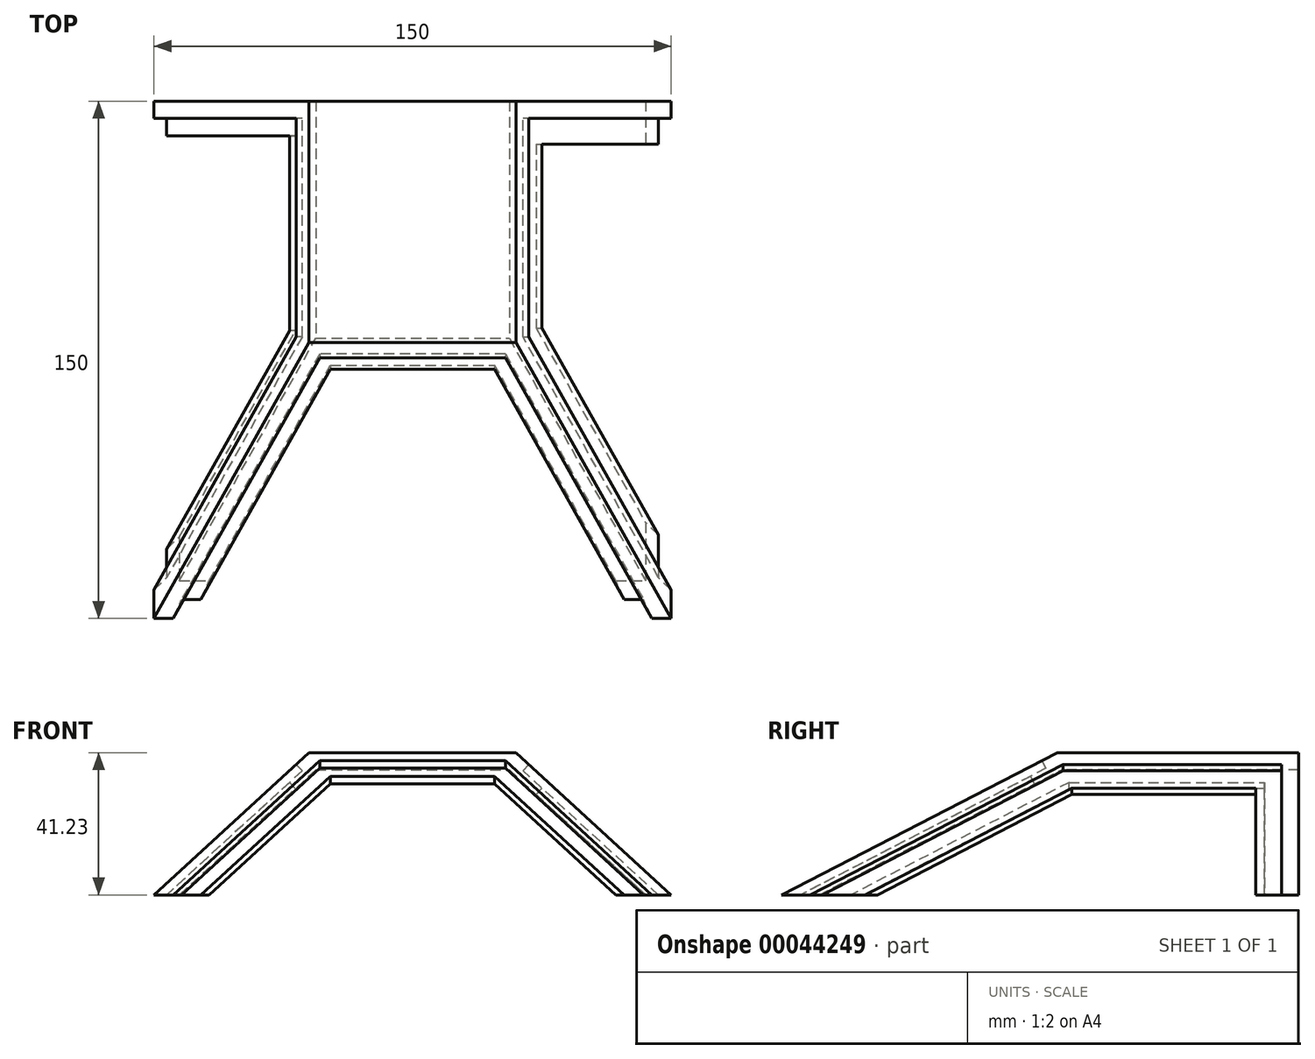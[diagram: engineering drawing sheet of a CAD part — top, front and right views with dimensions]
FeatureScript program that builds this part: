
annotation { "Feature Type Name" : "Feature", "Feature Type Description" : "" }
export const myFeature = defineFeature(function(context is Context, id is Id, definition is map)
    precondition{}
    {
        {
            var Q0;
            Q0=qCreatedBy(makeId("Top.planeOp"),FACE);
            var sketch = newSketch(context, id + "F0", { "sketchPlane" : qUnion([Q0])});
            skLineSegment(sketch, "E0.bottom", {"start": v(-75, 75) * mm, "end": v(75, 75) * mm});
            skLineSegment(sketch, "E0.top", {"start": v(-75, -75) * mm, "end": v(75, -75) * mm});
            skLineSegment(sketch, "E0.left", {"start": v(-75, 75) * mm, "end": v(-75, -75) * mm});
            skLineSegment(sketch, "E0.right", {"start": v(75, 75) * mm, "end": v(75, -75) * mm});
            skPoint(sketch, "E0.middle", {"position": v(0, 0) * mm});
            skLineSegment(sketch, "E1.bottom", {"start": v(30, 75) * mm, "end": v(-30, 75) * mm, "construction": true});
            skLineSegment(sketch, "E1.top", {"start": v(30, 5) * mm, "end": v(-30, 5) * mm, "construction": true});
            skLineSegment(sketch, "E1.left", {"start": v(30, 75) * mm, "end": v(30, 5) * mm, "construction": true});
            skLineSegment(sketch, "E1.right", {"start": v(-30, 75) * mm, "end": v(-30, 5) * mm, "construction": true});
            skPoint(sketch, "E1.middle", {"position": v(0, 40) * mm});
            skPoint(sketch, "E1.middle.positionSnap0", {"position": v(0, 75) * mm});
            skPoint(sketch, "E1.centerSnap0", {"position": v(0, 75) * mm});
            skLineSegment(sketch, "E2", {"start": v(-30, 40) * mm, "end": v(-75, 40) * mm, "construction": true});
            skLineSegment(sketch, "E3", {"start": v(30, 40) * mm, "end": v(75, 40) * mm, "construction": true});
            skLineSegment(sketch, "E4", {"start": v(30, 5) * mm, "end": v(75, -75) * mm, "construction": true});
            skSolve(sketch);
        }
        {
            var Q0;
            Q0=qCreatedBy(makeId("Right.planeOp"),FACE);
            var sketch = newSketch(context, id + "F1", { "sketchPlane" : qUnion([Q0])});
            skLineSegment(sketch, "E5.0", {"start": v(5, 0) * mm, "end": v(-75, 0) * mm, "construction": true});
            skLineSegment(sketch, "E6", {"start": v(-75, 0) * mm, "end": v(5, 41.23) * mm, "construction": true});
            skLineSegment(sketch, "E7", {"start": v(5, 41.23) * mm, "end": v(5, 0) * mm, "construction": true});
            skSolve(sketch);
        }
        {
            var Q0;
            Q0=sQuery(id+"F1.wireOp",EDGE,"E7");
            var Q1;
            Q1=sQuery(id+"F1.wireOp",VERTEX,"E6.end");
            cPlane(context, id + "F2", {"entities" : qUnion([Q0, Q1]), "cplaneType" : CPlaneType.CURVE_POINT, "offset" : 25 * mm, "width" : 150 * mm, "height" : 150 * mm});
        }
        {
            var Q0;
            Q0=qCreatedBy(id+"F2.planeOp",FACE);
            var sketch = newSketch(context, id + "F3", { "sketchPlane" : qUnion([Q0])});
            skLineSegment(sketch, "E8.0", {"start": v(-30, -75) * mm, "end": v(-30, -5) * mm});
            skLineSegment(sketch, "E9.0", {"start": v(30, -5) * mm, "end": v(-30, -5) * mm});
            skLineSegment(sketch, "E10.0", {"start": v(30, -75) * mm, "end": v(30, -5) * mm});
            skLineSegment(sketch, "E11.0", {"start": v(-75, -75) * mm, "end": v(75, -75) * mm});
            skSolve(sketch);
        }
        {
            var Q0;
            Q0=makeQuery(id+"F0.imprint","IMPRINT",FACE,{"disambiguationData":[TD([[makeQuery(id+"F0.imprint","IMPRINT",EDGE,{"derivedFrom":sQuery(id+"F0.wireOp",EDGE,"E0.bottom")}),-1.0]])]});
            var Q1;
            {var subQ0=sQuery(id+"F3.wireOp",EDGE,"E8.0");Q1=makeQuery(id+"F3.imprint","IMPRINT",FACE,{"disambiguationData":[TD([[makeQuery(id+"F3.imprint","IMPRINT",EDGE,{"derivedFrom":subQ0}),-1.0]])]});}
            var Q2;
            Q2=sQuery(id+"F0.wireOp",VERTEX,"E0.left.end");
            var Q3;
            Q3=sQuery(id+"F3.wireOp",VERTEX,"E8.0.start");
            loft(context, id + "F4", {"sheetProfilesArray" : [{ "sheetProfileEntities" : qUnion([Q0]) }, { "sheetProfileEntities" : qUnion([Q1]) }], "connections" : [{ "connectionEntities" : qUnion([Q2, Q3]), "connectionEdgeQueries" : qUnion([]), "connectionEdgeParameters" : [] }]});
        }
        {
            var Q0;
            Q0=makeQuery(id+"F4.opLoft","SWEPT_FACE",FACE,{"disambiguationData":[OSD([sQuery(id+"F0.wireOp",EDGE,"E0.bottom"),sQuery(id+"F0.wireOp",EDGE,"E0.left"),sQuery(id+"F0.wireOp",EDGE,"E0.right"),sQuery(id+"F3.wireOp",EDGE,"E8.0"),sQuery(id+"F3.wireOp",EDGE,"E10.0"),sQuery(id+"F3.wireOp",EDGE,"E11.0")])]});
            var Q1;
            Q1=makeQuery(id+"F4.opLoft","CAP_FACE",FACE,{"disambiguationData":[OSD([makeQuery(id+"F0.imprint","IMPRINT",FACE,{"disambiguationData":[TD([[makeQuery(id+"F0.imprint","IMPRINT",EDGE,{"derivedFrom":sQuery(id+"F0.wireOp",EDGE,"E0.bottom")}),-1.0]])]})])],"isStart":true});
            shell(context, id + "F5", {"entities" : qUnion([Q0, Q1]), "thickness" : 5 * mm});
        }
        {
            var Q0;
            Q0=makeQuery(id+"F4.opLoft","SWEPT_FACE",FACE,{"disambiguationData":[OSD([sQuery(id+"F0.wireOp",EDGE,"E0.bottom"),sQuery(id+"F0.wireOp",EDGE,"E0.top"),sQuery(id+"F0.wireOp",EDGE,"E0.right"),sQuery(id+"F3.wireOp",EDGE,"E9.0"),sQuery(id+"F3.wireOp",EDGE,"E10.0"),sQuery(id+"F3.wireOp",EDGE,"E11.0")])]});
            var sketch = newSketch(context, id + "F6", { "sketchPlane" : qUnion([Q0])});
            skLineSegment(sketch, "E12.0", {"start": v(55.3, 70) * mm, "end": v(-0.73, 70) * mm});
            skLineSegment(sketch, "E12.1", {"start": v(-0.73, 6.69) * mm, "end": v(-0.73, 70) * mm});
            skLineSegment(sketch, "E12.2", {"start": v(59.27, -71.97) * mm, "end": v(-0.73, 6.69) * mm});
            skLineSegment(sketch, "E13.0", {"start": v(55.3, 62.5) * mm, "end": v(6.77, 62.5) * mm});
            skLineSegment(sketch, "E13.1", {"start": v(6.77, 9.22) * mm, "end": v(6.77, 62.5) * mm});
            skLineSegment(sketch, "E13.2", {"start": v(65.24, -67.42) * mm, "end": v(6.77, 9.22) * mm});
            skSolve(sketch);
        }
        {
            var Q0;
            {var subQ7=sQuery(id+"F6.wireOp",EDGE,"E12.0");Q0=makeQuery(id+"F6.imprint","IMPRINT",FACE,{"disambiguationData":[TD([[makeQuery(id+"F6.imprint","IMPRINT",EDGE,{"derivedFrom":subQ7}),1.0]])]});}
            var Q1;
            Q1=makeQuery(id+"F5.opShell","OFFSET_FACE",FACE,{"disambiguationData":[OSD([sQuery(id+"F0.wireOp",EDGE,"E0.bottom"),sQuery(id+"F0.wireOp",EDGE,"E0.top"),sQuery(id+"F0.wireOp",EDGE,"E0.right"),sQuery(id+"F3.wireOp",EDGE,"E9.0"),sQuery(id+"F3.wireOp",EDGE,"E10.0"),sQuery(id+"F3.wireOp",EDGE,"E11.0")])]});
            extrude(context, id + "F7", {"entities" : qUnion([Q0]), "operationType" : NewBodyOperationType.REMOVE, "endBound" : BoundingType.UP_TO_SURFACE, "oppositeDirection" : true, "depth" : 25 * mm, "endBoundEntityFace" : qUnion([Q1]), "hasOffset" : true, "offsetDistance" : 2.5 * mm});
        }
        {
            var Q0;
            {var subQ0=sQuery(id+"F0.wireOp",EDGE,"E0.bottom");var subQ1=sQuery(id+"F0.wireOp",EDGE,"E0.top");var subQ2=sQuery(id+"F0.wireOp",EDGE,"E0.right");Q0=makeQuery(id+"F7.boolean.opBoolean","SPLIT",FACE,{"disambiguationData":[TD([makeQuery(id+"F7.opExtrude","SWEPT_FACE",FACE,{"disambiguationData":[OSD([sQuery(id+"F6.wireOp",EDGE,"E13.0")])]})])],"derivedFrom":makeQuery(id+"F4.opLoft","SWEPT_FACE",FACE,{"disambiguationData":[OSD([subQ0,subQ1,subQ2,sQuery(id+"F3.wireOp",EDGE,"E9.0"),sQuery(id+"F3.wireOp",EDGE,"E10.0"),sQuery(id+"F3.wireOp",EDGE,"E11.0")])]})});}
            extrude(context, id + "F8", {"entities" : qUnion([Q0]), "operationType" : NewBodyOperationType.REMOVE, "endBound" : BoundingType.THROUGH_ALL, "oppositeDirection" : true, "depth" : 25 * mm, "offsetDistance" : 25 * mm});
        }
        {
            var Q0;
            Q0=makeQuery(id+"F4.opLoft","SWEPT_FACE",FACE,{"disambiguationData":[OSD([sQuery(id+"F0.wireOp",EDGE,"E0.top"),sQuery(id+"F0.wireOp",EDGE,"E0.left"),sQuery(id+"F0.wireOp",EDGE,"E0.right"),sQuery(id+"F3.wireOp",EDGE,"E8.0"),sQuery(id+"F3.wireOp",EDGE,"E9.0"),sQuery(id+"F3.wireOp",EDGE,"E10.0")])]});
            var sketch = newSketch(context, id + "F9", { "sketchPlane" : qUnion([Q0])});
            skLineSegment(sketch, "E14.0", {"start": v(70.53, -68.9) * mm, "end": v(26.9, 18.33) * mm});
            skLineSegment(sketch, "E14.1", {"start": v(-26.9, 18.33) * mm, "end": v(26.9, 18.33) * mm});
            skLineSegment(sketch, "E14.2", {"start": v(-70.53, -68.9) * mm, "end": v(-26.9, 18.33) * mm});
            skLineSegment(sketch, "E15.0", {"start": v(66.06, -71.14) * mm, "end": v(23.82, 13.33) * mm});
            skLineSegment(sketch, "E15.1", {"start": v(-23.82, 13.33) * mm, "end": v(23.82, 13.33) * mm});
            skLineSegment(sketch, "E15.2", {"start": v(-66.06, -71.14) * mm, "end": v(-23.82, 13.33) * mm});
            skSolve(sketch);
        }
        {
            var Q0;
            {var subQ0=sQuery(id+"F9.wireOp",EDGE,"E15.1");Q0=makeQuery(id+"F9.imprint","IMPRINT",FACE,{"disambiguationData":[TD([[makeQuery(id+"F9.imprint","IMPRINT",EDGE,{"derivedFrom":subQ0}),-1.0]])]});}
            extrude(context, id + "F10", {"entities" : qUnion([Q0]), "operationType" : NewBodyOperationType.REMOVE, "endBound" : BoundingType.THROUGH_ALL, "oppositeDirection" : true, "depth" : 25 * mm, "offsetDistance" : 25 * mm});
        }
        {
            var Q0;
            {var subQ5=sQuery(id+"F9.wireOp",EDGE,"E14.1");Q0=makeQuery(id+"F9.imprint","IMPRINT",FACE,{"disambiguationData":[TD([[makeQuery(id+"F9.imprint","IMPRINT",EDGE,{"derivedFrom":subQ5}),-1.0]])]});}
            var Q1;
            Q1=makeQuery(id+"F5.opShell","OFFSET_FACE",FACE,{"disambiguationData":[OSD([sQuery(id+"F0.wireOp",EDGE,"E0.top"),sQuery(id+"F0.wireOp",EDGE,"E0.left"),sQuery(id+"F0.wireOp",EDGE,"E0.right"),sQuery(id+"F3.wireOp",EDGE,"E8.0"),sQuery(id+"F3.wireOp",EDGE,"E9.0"),sQuery(id+"F3.wireOp",EDGE,"E10.0")])]});
            extrude(context, id + "F11", {"entities" : qUnion([Q0]), "operationType" : NewBodyOperationType.REMOVE, "endBound" : BoundingType.UP_TO_SURFACE, "oppositeDirection" : true, "depth" : 25 * mm, "endBoundEntityFace" : qUnion([Q1]), "hasOffset" : true, "offsetDistance" : 2.5 * mm});
        }
        {
            var Q0;
            Q0=makeQuery(id+"F4.opLoft","SWEPT_FACE",FACE,{"disambiguationData":[OSD([sQuery(id+"F0.wireOp",EDGE,"E0.bottom"),sQuery(id+"F0.wireOp",EDGE,"E0.top"),sQuery(id+"F0.wireOp",EDGE,"E0.left"),sQuery(id+"F3.wireOp",EDGE,"E8.0"),sQuery(id+"F3.wireOp",EDGE,"E9.0"),sQuery(id+"F3.wireOp",EDGE,"E11.0")])]});
            var sketch = newSketch(context, id + "F12", { "sketchPlane" : qUnion([Q0])});
            skLineSegment(sketch, "E16.0", {"start": v(-59.27, -71.97) * mm, "end": v(0.73, 6.69) * mm});
            skLineSegment(sketch, "E16.1", {"start": v(0.73, 70) * mm, "end": v(0.73, 6.69) * mm});
            skLineSegment(sketch, "E16.2", {"start": v(-55.3, 70) * mm, "end": v(0.73, 70) * mm});
            skLineSegment(sketch, "E17.0", {"start": v(-63.25, -68.93) * mm, "end": v(-4.27, 8.38) * mm});
            skLineSegment(sketch, "E17.1", {"start": v(-4.27, 65) * mm, "end": v(-4.27, 8.38) * mm});
            skLineSegment(sketch, "E17.2", {"start": v(-55.3, 65) * mm, "end": v(-4.27, 65) * mm});
            skSolve(sketch);
        }
        {
            var Q0;
            {var subQ7=sQuery(id+"F12.wireOp",EDGE,"E16.1");Q0=makeQuery(id+"F12.imprint","IMPRINT",FACE,{"disambiguationData":[TD([[makeQuery(id+"F12.imprint","IMPRINT",EDGE,{"derivedFrom":subQ7}),-1.0]])]});}
            var Q1;
            Q1=makeQuery(id+"F5.opShell","OFFSET_FACE",FACE,{"disambiguationData":[OSD([sQuery(id+"F0.wireOp",EDGE,"E0.bottom"),sQuery(id+"F0.wireOp",EDGE,"E0.top"),sQuery(id+"F0.wireOp",EDGE,"E0.left"),sQuery(id+"F3.wireOp",EDGE,"E8.0"),sQuery(id+"F3.wireOp",EDGE,"E9.0"),sQuery(id+"F3.wireOp",EDGE,"E11.0")])]});
            extrude(context, id + "F13", {"entities" : qUnion([Q0]), "operationType" : NewBodyOperationType.REMOVE, "endBound" : BoundingType.UP_TO_SURFACE, "oppositeDirection" : true, "depth" : 25 * mm, "endBoundEntityFace" : qUnion([Q1]), "hasOffset" : true, "offsetDistance" : 2.5 * mm});
        }
        {
            var Q0;
            {var subQ0=sQuery(id+"F0.wireOp",EDGE,"E0.bottom");var subQ1=sQuery(id+"F0.wireOp",EDGE,"E0.top");var subQ2=sQuery(id+"F0.wireOp",EDGE,"E0.left");Q0=makeQuery(id+"F13.boolean.opBoolean","SPLIT",FACE,{"disambiguationData":[TD([makeQuery(id+"F13.opExtrude","SWEPT_FACE",FACE,{"disambiguationData":[OSD([sQuery(id+"F12.wireOp",EDGE,"E17.0")])]})])],"derivedFrom":makeQuery(id+"F4.opLoft","SWEPT_FACE",FACE,{"disambiguationData":[OSD([subQ0,subQ1,subQ2,sQuery(id+"F3.wireOp",EDGE,"E8.0"),sQuery(id+"F3.wireOp",EDGE,"E9.0"),sQuery(id+"F3.wireOp",EDGE,"E11.0")])]})});}
            extrude(context, id + "F14", {"entities" : qUnion([Q0]), "operationType" : NewBodyOperationType.REMOVE, "endBound" : BoundingType.THROUGH_ALL, "oppositeDirection" : true, "depth" : 25 * mm, "offsetDistance" : 25 * mm});
        }
    });
